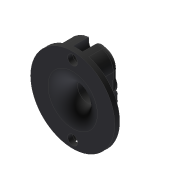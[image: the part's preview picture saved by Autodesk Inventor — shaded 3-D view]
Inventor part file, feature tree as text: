
AUTODESK INVENTOR PART (.ipt)
format: ipt  version: 2017 (Build 210142000, 142)  size: 253,952 bytes
history: native  units: mm
features: sketch x7, extrude x6, fillet x4, projected_geometry x2, hole x1, chamfer x1
ambient origin geometry x8: Origin, YZ Plane, XZ Plane, XY Plane, X Axis, Y Axis, Z Axis, Center Point
bodies: Solid1 (feature_tree)
feature tree (21):
  extrude  "Extrusion1"  Depth=2.0mm TaperAngle=0.0deg
  extrude  "Extrusion2"  Depth=3.5mm
  fillet  "Fillet1"  Radius=3.5mm
  extrude  "Extrusion3"  Depth=2.0mm
  extrude  "Extrusion4"  Depth=2.0mm TaperAngle=0.0deg
  hole  "Hole1"  [1 undecoded]
  fillet  "Fillet2"  Radius=14.0mm
  extrude  "Extrusion5"  Depth=6.0mm
  chamfer  "Chamfer1"  Distance=18.0mm
  extrude  "Extrusion6"  Depth=2.5mm TaperAngle=0.0deg
  fillet  "Fillet3"  Radius=8.0mm
  fillet  "Fillet4"  Radius=7.0mm
  sketch  "Sketch1"  dims[d0=34.0mm d1=2.0mm d2=0.0mm]
  sketch  "Sketch2"  dims[d3=8.0mm d4=5.5mm d5=3.5mm]
  sketch  "Sketch3"  dims[d6=4.0mm d7=0.0mm d8=2.0mm]
  sketch  "Sketch4"  dims[d9=8.0mm d10=2.0mm d11=0.0mm]
  projected_geometry  "Projected Loop1"
  sketch  "Sketch5"  dims[d12=8.0mm d13=0.0mm d14=14.0mm d15=14.0mm]
  sketch  "Sketch6"  dims[d16=4.0mm d17=6.0mm d18=4.0mm d19=2.0mm d20=90.0deg d21=8.0mm d22=20.594885mm d23=6.0mm]
  sketch  "Sketch7"  dims[d24=18.0mm d25=18.0mm d26=8.0mm d27=0.0mm d28=8.0mm d29=2.0mm d30=45.0deg d31=7.0mm d32=7.0mm d33=8.0mm d34=0.0mm d35=6.0mm d36=2.5mm]
  projected_geometry  "Projected Loop2"
note: 1 required parameter value undecoded (feature->parameter linkage not recoverable at this tier; creation-order binding heuristic only, values carry confidence <= 0.55)
